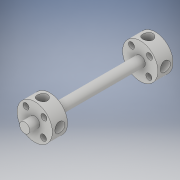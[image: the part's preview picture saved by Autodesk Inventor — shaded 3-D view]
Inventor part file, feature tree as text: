
AUTODESK INVENTOR PART (.ipt)
format: ipt  version: 2019 (Build 230136000, 136)  size: 187,392 bytes
history: native  units: in
note: dims shown in document units (in); Inventor stores cm internally (conversion verified against a paired STEP export)
features: sketch x5, extrude x3, hole x2, pattern_circular x2, plane x1, mirror x1, projected_geometry x1
ambient origin geometry x8: Origin, YZ Plane, XZ Plane, XY Plane, X Axis, Y Axis, Z Axis, Center Point
bodies: Solid1 (feature_tree)
feature tree (15):
  extrude  "Extrusion2"  Depth=0.375in TaperAngle=0.0deg
  extrude  "Extrusion3"  Depth=1.12in TaperAngle=0.0deg
  hole  "Hole2"  [1 undecoded]
  pattern_circular  "Circular Pattern2"  Count=4 Angle=360.0deg
  plane  "Work Plane2"
  hole  "Hole3"  [1 undecoded]
  pattern_circular  "Circular Pattern3"  [2 undecoded]
  mirror  "Mirror1"
  extrude  "Extrusion4"  Depth=0.25in TaperAngle=0.0deg
  sketch  "Sketch2"  dims[d6=0.875in d7=0.375in d8=0.0in]
  sketch  "Sketch6"  dims[d17=0.25in d18=1.12in d19=0.0in]
  sketch  "Sketch7"  dims[d20=0.315in]
  projected_geometry  "Projected Loop1"
  sketch  "Sketch8"  dims[d21=0.15in d22=0.75in d23=0.375in d24=0.25in d25=0.5635in d26=1.0in d27=0.8108in d28=1.5748in d29=360.0deg]
  sketch  "Sketch9"  dims[d31=0.4375in d32=0.25in d33=0.75in d34=0.375in d35=0.25in d36=0.5635in d37=1.0in d38=0.8108in d39=1.5748in d40=360.0deg d42=45.0deg d43=0.25in d44=0.25in d45=0.0in]
note: 4 required parameter values undecoded (feature->parameter linkage not recoverable at this tier; creation-order binding heuristic only, values carry confidence <= 0.55)
